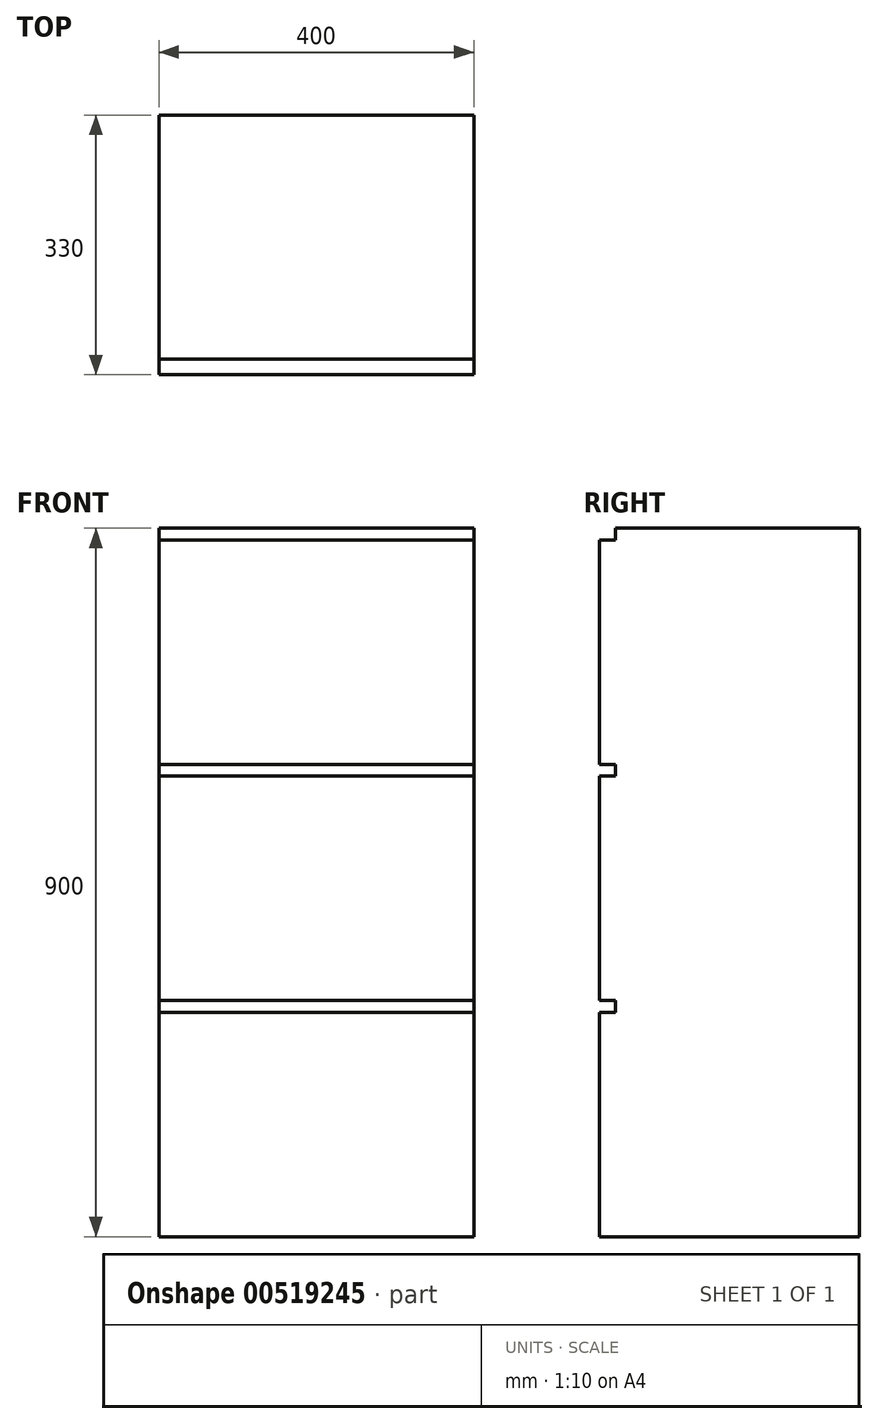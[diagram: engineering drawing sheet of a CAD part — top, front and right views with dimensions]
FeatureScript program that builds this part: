
annotation { "Feature Type Name" : "Feature", "Feature Type Description" : "" }
export const myFeature = defineFeature(function(context is Context, id is Id, definition is map)
    precondition{}
    {
        {
            var Q0;
            Q0=qCreatedBy(makeId("Right.planeOp"),FACE);
            var sketch = newSketch(context, id + "F0", { "sketchPlane" : qUnion([Q0])});
            skLineSegment(sketch, "E0.bottom", {"start": v(0, 0) * mm, "end": v(330, 0) * mm});
            skLineSegment(sketch, "E0.top", {"start": v(0, 900) * mm, "end": v(330, 900) * mm});
            skLineSegment(sketch, "E0.left", {"start": v(0, 0) * mm, "end": v(0, 900) * mm});
            skLineSegment(sketch, "E0.right", {"start": v(330, 0) * mm, "end": v(330, 900) * mm});
            skSolve(sketch);
        }
        {
            var Q0;
            Q0 = qSketchRegion(id + "F0", true);
            extrude(context, id + "F1", {"entities" : qUnion([Q0]), "depth" : 400 * mm, "offsetDistance" : 25 * mm});
        }
        {
            var Q0;
            Q0=makeQuery(id+"F1.opExtrude","SWEPT_FACE",FACE,{"disambiguationData":[OSD([sQuery(id+"F0.wireOp",EDGE,"E0.left")])]});
            var sketch = newSketch(context, id + "F2", { "sketchPlane" : qUnion([Q0])});
            skLineSegment(sketch, "E1.bottom", {"start": v(0, 900) * mm, "end": v(400, 900) * mm});
            skLineSegment(sketch, "E1.top", {"start": v(0, 885) * mm, "end": v(400, 885) * mm});
            skLineSegment(sketch, "E1.left", {"start": v(0, 900) * mm, "end": v(0, 885) * mm});
            skLineSegment(sketch, "E1.right", {"start": v(400, 900) * mm, "end": v(400, 885) * mm});
            skLineSegment(sketch, "E2.0.1.0", {"start": v(0, 600) * mm, "end": v(400, 600) * mm});
            skLineSegment(sketch, "E2.0.1.1", {"start": v(0, 585) * mm, "end": v(400, 585) * mm});
            skLineSegment(sketch, "E2.0.1.2", {"start": v(400, 600) * mm, "end": v(400, 585) * mm});
            skLineSegment(sketch, "E2.0.1.3", {"start": v(0, 600) * mm, "end": v(0, 585) * mm});
            skLineSegment(sketch, "E2.0.2.0", {"start": v(0, 300) * mm, "end": v(400, 300) * mm});
            skLineSegment(sketch, "E2.0.2.1", {"start": v(0, 285) * mm, "end": v(400, 285) * mm});
            skLineSegment(sketch, "E2.0.2.2", {"start": v(400, 300) * mm, "end": v(400, 285) * mm});
            skLineSegment(sketch, "E2.0.2.3", {"start": v(0, 300) * mm, "end": v(0, 285) * mm});
            skLineSegment(sketch, "E2.direction1", {"start": v(0, 885) * mm, "end": v(25, 885) * mm, "construction": true});
            skLineSegment(sketch, "E2.direction2", {"start": v(0, 885) * mm, "end": v(0, 585) * mm, "construction": true});
            skSolve(sketch);
        }
        {
            var Q0;
            Q0 = qSketchRegion(id + "F2", true);
            var Q1;
            Q1=makeQuery(id+"F2.imprint","IMPRINT",FACE,{"disambiguationData":[TD([[makeQuery(id+"F2.imprint","IMPRINT",EDGE,{"derivedFrom":sQuery(id+"F2.wireOp",EDGE,"t5xuRjhr-ihwX-vWyE-7tZp-QTPIxSL2vUkp")}),1.0]])]});
            var Q2;
            Q2=makeQuery(id+"F2.imprint","IMPRINT",FACE,{"disambiguationData":[TD([[makeQuery(id+"F2.imprint","IMPRINT",EDGE,{"derivedFrom":sQuery(id+"F2.wireOp",EDGE,"KuJuSUFt-iiOn-ht2h-YZWW-18KYoQS2msUA")}),1.0]])]});
            var Q3;
            Q3=makeQuery(id+"F2.imprint","IMPRINT",FACE,{"disambiguationData":[TD([[makeQuery(id+"F2.imprint","IMPRINT",EDGE,{"derivedFrom":sQuery(id+"F2.wireOp",EDGE,"40cc373c-1c27-49f5-a3b0-167c6d5d02f6.0.1.0")}),1.0]])]});
            var Q4;
            Q4=makeQuery(id+"F2.imprint","IMPRINT",FACE,{"disambiguationData":[TD([[makeQuery(id+"F2.imprint","IMPRINT",EDGE,{"derivedFrom":sQuery(id+"F2.wireOp",EDGE,"40cc373c-1c27-49f5-a3b0-167c6d5d02f6.0.1.1")}),1.0]])]});
            var Q5;
            Q5=makeQuery(id+"F2.imprint","IMPRINT",FACE,{"disambiguationData":[TD([[makeQuery(id+"F2.imprint","IMPRINT",EDGE,{"derivedFrom":sQuery(id+"F2.wireOp",EDGE,"40cc373c-1c27-49f5-a3b0-167c6d5d02f6.0.2.0")}),1.0]])]});
            var Q6;
            Q6=makeQuery(id+"F2.imprint","IMPRINT",FACE,{"disambiguationData":[TD([[makeQuery(id+"F2.imprint","IMPRINT",EDGE,{"derivedFrom":sQuery(id+"F2.wireOp",EDGE,"40cc373c-1c27-49f5-a3b0-167c6d5d02f6.0.2.1")}),1.0]])]});
            var Q7;
            Q7=makeQuery(id+"F2.imprint","IMPRINT",FACE,{"disambiguationData":[TD([[makeQuery(id+"F2.imprint","IMPRINT",EDGE,{"derivedFrom":sQuery(id+"F2.wireOp",EDGE,"40cc373c-1c27-49f5-a3b0-167c6d5d02f6.0.3.0")}),1.0]])]});
            var Q8;
            Q8=makeQuery(id+"F2.imprint","IMPRINT",FACE,{"disambiguationData":[TD([[makeQuery(id+"F2.imprint","IMPRINT",EDGE,{"derivedFrom":sQuery(id+"F2.wireOp",EDGE,"40cc373c-1c27-49f5-a3b0-167c6d5d02f6.0.3.1")}),1.0]])]});
            extrude(context, id + "F3", {"entities" : qUnion([Q0, Q1, Q2, Q3, Q4, Q5, Q6, Q7, Q8]), "operationType" : NewBodyOperationType.REMOVE, "oppositeDirection" : true, "depth" : 20 * mm, "offsetDistance" : 25 * mm});
        }
    });
